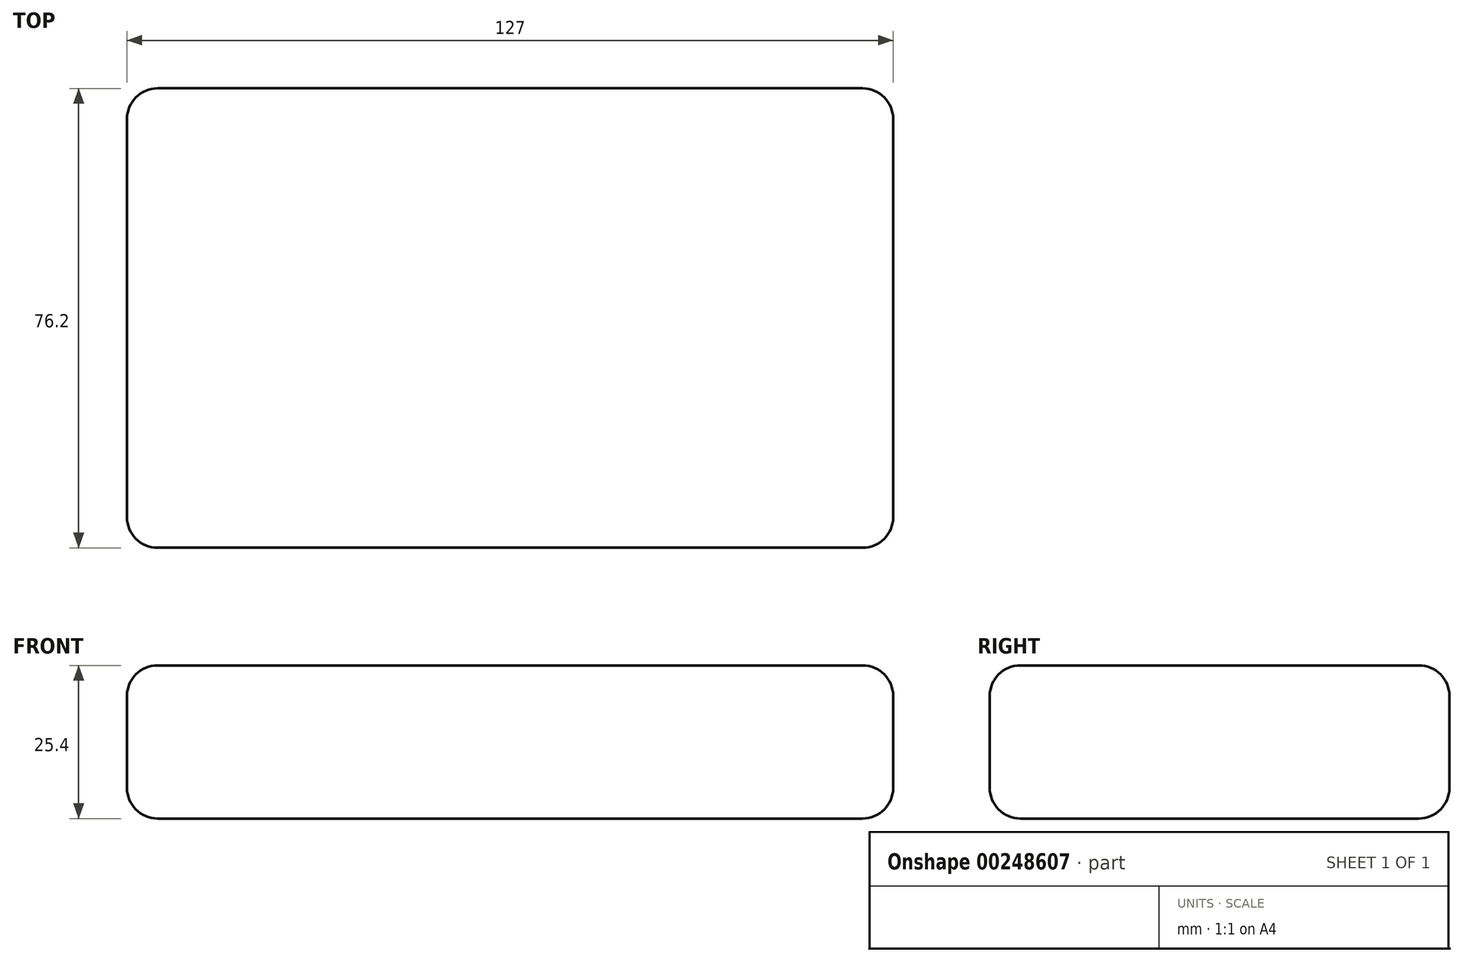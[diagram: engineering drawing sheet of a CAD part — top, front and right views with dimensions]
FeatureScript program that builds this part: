
annotation { "Feature Type Name" : "Feature", "Feature Type Description" : "" }
export const myFeature = defineFeature(function(context is Context, id is Id, definition is map)
    precondition{}
    {
        {
            var Q0;
            Q0=qCreatedBy(makeId("Top.planeOp"),FACE);
            var sketch = newSketch(context, id + "F0", { "sketchPlane" : qUnion([Q0])});
            skLineSegment(sketch, "E0.bottom", {"start": v(-65.1, 41.51) * mm, "end": v(61.9, 41.51) * mm});
            skLineSegment(sketch, "E0.top", {"start": v(-65.1, -34.69) * mm, "end": v(61.9, -34.69) * mm});
            skLineSegment(sketch, "E0.left", {"start": v(-65.1, 41.51) * mm, "end": v(-65.1, -34.69) * mm});
            skLineSegment(sketch, "E0.right", {"start": v(61.9, 41.51) * mm, "end": v(61.9, -34.69) * mm});
            skSolve(sketch);
        }
        {
            var Q0;
            Q0 = qSketchRegion(id + "F0", true);
            extrude(context, id + "F1", {"entities" : qUnion([Q0]), "depth" : 25.4 * mm});
        }
        {
            var Q0;
            Q0=makeQuery(id+"F1.opExtrude","CAP_EDGE",EDGE,{"disambiguationData":[OSD([sQuery(id+"F0.wireOp",EDGE,"E0.top")])],"isStart":false});
            var Q1;
            Q1=makeQuery(id+"F1.opExtrude","CAP_EDGE",EDGE,{"disambiguationData":[OSD([sQuery(id+"F0.wireOp",EDGE,"E0.right")])],"isStart":false});
            var Q2;
            Q2=makeQuery(id+"F1.opExtrude","SWEPT_EDGE",EDGE,{"disambiguationData":[OSD([sQuery(id+"F0.wireOp",EDGE,"E0.top"),sQuery(id+"F0.wireOp",EDGE,"E0.right")])]});
            fillet(context, id + "F2", {"entities" : qUnion([Q0, Q1, Q2]), "radius" : 5.08 * mm, "tangentPropagation" : true, "allowEdgeOverflow" : false});
        }
        {
            var Q0;
            Q0=makeQuery(id+"F1.opExtrude","CAP_EDGE",EDGE,{"disambiguationData":[OSD([sQuery(id+"F0.wireOp",EDGE,"E0.left")])],"isStart":false});
            var Q1;
            Q1=makeQuery(id+"F1.opExtrude","SWEPT_EDGE",EDGE,{"disambiguationData":[OSD([sQuery(id+"F0.wireOp",EDGE,"E0.top"),sQuery(id+"F0.wireOp",EDGE,"E0.left")])]});
            var Q2;
            Q2=makeQuery(id+"F1.opExtrude","CAP_EDGE",EDGE,{"disambiguationData":[OSD([sQuery(id+"F0.wireOp",EDGE,"E0.left")])],"isStart":true});
            var Q3;
            Q3=makeQuery(id+"F1.opExtrude","CAP_EDGE",EDGE,{"disambiguationData":[OSD([sQuery(id+"F0.wireOp",EDGE,"E0.top")])],"isStart":true});
            fillet(context, id + "F3", {"entities" : qUnion([Q0, Q1, Q2, Q3]), "radius" : 5.08 * mm, "tangentPropagation" : true, "allowEdgeOverflow" : false});
        }
        {
            var Q0;
            Q0=makeQuery(id+"F1.opExtrude","CAP_EDGE",EDGE,{"disambiguationData":[OSD([sQuery(id+"F0.wireOp",EDGE,"E0.bottom")])],"isStart":true});
            var Q1;
            Q1=makeQuery(id+"F1.opExtrude","SWEPT_EDGE",EDGE,{"disambiguationData":[OSD([sQuery(id+"F0.wireOp",EDGE,"E0.bottom"),sQuery(id+"F0.wireOp",EDGE,"E0.right")])]});
            var Q2;
            Q2=makeQuery(id+"F1.opExtrude","CAP_EDGE",EDGE,{"disambiguationData":[OSD([sQuery(id+"F0.wireOp",EDGE,"E0.bottom")])],"isStart":false});
            var Q3;
            Q3=makeQuery(id+"F1.opExtrude","SWEPT_EDGE",EDGE,{"disambiguationData":[OSD([sQuery(id+"F0.wireOp",EDGE,"E0.bottom"),sQuery(id+"F0.wireOp",EDGE,"E0.left")])]});
            fillet(context, id + "F4", {"entities" : qUnion([Q0, Q1, Q2, Q3]), "radius" : 5.08 * mm, "tangentPropagation" : true, "allowEdgeOverflow" : false});
        }
    });
